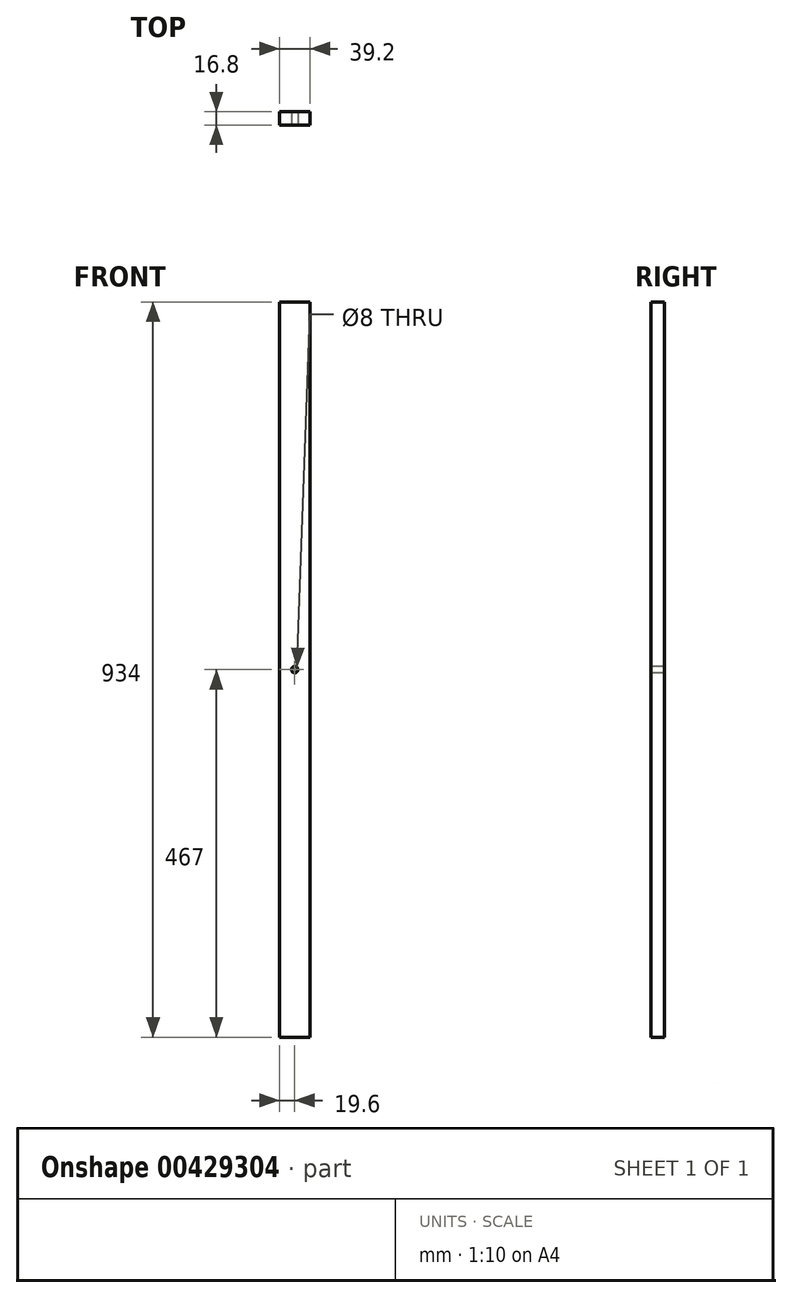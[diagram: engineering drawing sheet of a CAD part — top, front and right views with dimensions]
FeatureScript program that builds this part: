
annotation { "Feature Type Name" : "Feature", "Feature Type Description" : "" }
export const myFeature = defineFeature(function(context is Context, id is Id, definition is map)
    precondition{}
    {
        {
            var Q0;
            Q0=qCreatedBy(makeId("Top.planeOp"),FACE);
            var sketch = newSketch(context, id + "F0", { "sketchPlane" : qUnion([Q0])});
            skLineSegment(sketch, "E0.bottom", {"start": v(19.6, -8.4) * mm, "end": v(-19.6, -8.4) * mm});
            skLineSegment(sketch, "E0.top", {"start": v(19.6, 8.4) * mm, "end": v(-19.6, 8.4) * mm});
            skLineSegment(sketch, "E0.left", {"start": v(19.6, -8.4) * mm, "end": v(19.6, 8.4) * mm});
            skLineSegment(sketch, "E0.right", {"start": v(-19.6, -8.4) * mm, "end": v(-19.6, 8.4) * mm});
            skPoint(sketch, "E0.middle", {"position": v(0, 0) * mm});
            skSolve(sketch);
        }
        {
            var Q0;
            Q0=makeQuery(id+"F0.imprint","IMPRINT",FACE,{"disambiguationData":[TD([[makeQuery(id+"F0.imprint","IMPRINT",EDGE,{"derivedFrom":sQuery(id+"F0.wireOp",EDGE,"E0.bottom")}),-1.0]])]});
            extrude(context, id + "F1", {"entities" : qUnion([Q0]), "depth" : 934 * mm});
        }
        {
            var Q0;
            Q0=makeQuery(id+"F1.opExtrude","SWEPT_FACE",FACE,{"disambiguationData":[OSD([sQuery(id+"F0.wireOp",EDGE,"E0.bottom")])]});
            var sketch = newSketch(context, id + "F2", { "sketchPlane" : qUnion([Q0])});
            skLineSegment(sketch, "E1", {"start": v(0, 934) * mm, "end": v(0, 0) * mm, "construction": true});
            skCircle(sketch, "E2", {"center": v(0, 467) * mm, "radius": 4 * mm});
            skSolve(sketch);
        }
        {
            var Q0;
            Q0=makeQuery(id+"F2.imprint","IMPRINT",FACE,{"disambiguationData":[TD([[makeQuery(id+"F2.imprint","IMPRINT",EDGE,{"derivedFrom":sQuery(id+"F2.wireOp",EDGE,"E2")}),1.0]])]});
            extrude(context, id + "F3", {"entities" : qUnion([Q0]), "operationType" : NewBodyOperationType.REMOVE, "endBound" : BoundingType.UP_TO_NEXT, "oppositeDirection" : true, "depth" : 25 * mm});
        }
    });
